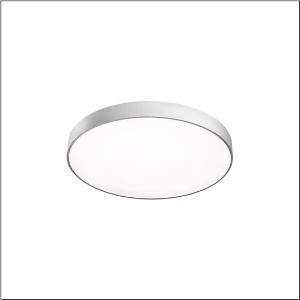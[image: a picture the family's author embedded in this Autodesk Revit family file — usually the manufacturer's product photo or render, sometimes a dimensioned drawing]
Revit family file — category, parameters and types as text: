
# Revit family: round_21_m_51mr36gm8421s
name_source: partatom
category: Lighting Fixtures
units: mm (PartAtom-declared; Revit-internal decimal feet)

## family parameters
Cut with Voids When Loaded = No
Host = Face
Light Source = No
Part Type = Normal
Room Calculation Point = No
Round Connector Dimension = Use Diameter
Shared = No

## types (1)
- --- (1 x LED, 8960 lm, 62.3 W, 4000K)
    Apparent Load = 62 VA
    CIE Flux Codes = 49 80 96 85 100
    Color Rendering = 80
    Color Temperature = 4000K
    Default Elevation = 1800 mm
    Description = Round 21 M, wall and ceiling luminaire, primary optical cover: cover, of PMMA, opal, light emission: direct/indirect distribution, primary light characteristic: symmetric, installation type: suspended mounting, surface-mounted, LED, rated luminous flux: 8.190lm, luminous efficacy: 135lm/W, light colour: 840, colour temperature: 4000K, control gear: ON/OFF Multilumen, with terminal, 3-pole, mains connection: 230V, AC, 50/60Hz, rated input power: 61W, housing, of aluminium, coated, silver, diameter: 600mm, height: 62mm, protection rating (complete): IP40, insulation class (complete): insulation class I (protective earthing), certification: CE, impact resistance: IK04, permissible operating ambient temperature: -10..+35°C, packaging unit: 1 piece
    Height = 87 mm
    Lamp = 1 x LED
    Lamp Light Flux = 8960 lm
    Lamp Power = 62.3 W
    Lamp count = 1
    Length = 600 mm
    Luminous efficacy = 144 lm/W
    Manufacturer = Siteco
    ModVariant = No
    Model = 51MR36GM8421S
    Mounting Place = Ceiling
    Mounting Type = Surface mounted
    Number of Poles = 1
    OnlyDefault = Yes
    Power Factor = 1
    Product Name = Round 21 M
    Product group = wall and ceiling luminaire | ceiling mounted
    ProductGroupID = 304
    Protection Class = Protection class I
    Protection Degree = IP 40
    RLX_Detail_Level = 1
    RLX_Emergency_Light_Flux = 0 lm
    RLX_Emergency_Type = 0
    RLX_Emergency_Type_DB = No
    RlxData = <blob elided: 17929 chars, md5=f881bf63>
    Socket = socket
    Standby Power = 0 W
    System Light Flux = 8960 lm
    System Power = 62 W
    Type Comments = factory setting: luminous flux: 100 % | (ON | ON | ON | ON) | 700 mA
    Type Image = l_1258303.jpg
    URL = http://relux.com
    VarID = @adj_040819
    Voltage = 0 V
    Weight = 0.00 kg
    Width = 0 mm  [stored 0 ft]

note: [stored X ft] marks values corroborated as IEEE doubles in the binary element streams (Revit-internal decimal feet)

## geometry (parser evidence)
native form markers: Blend x4, Sweep x13
no freeform markers — native parametric forms only
